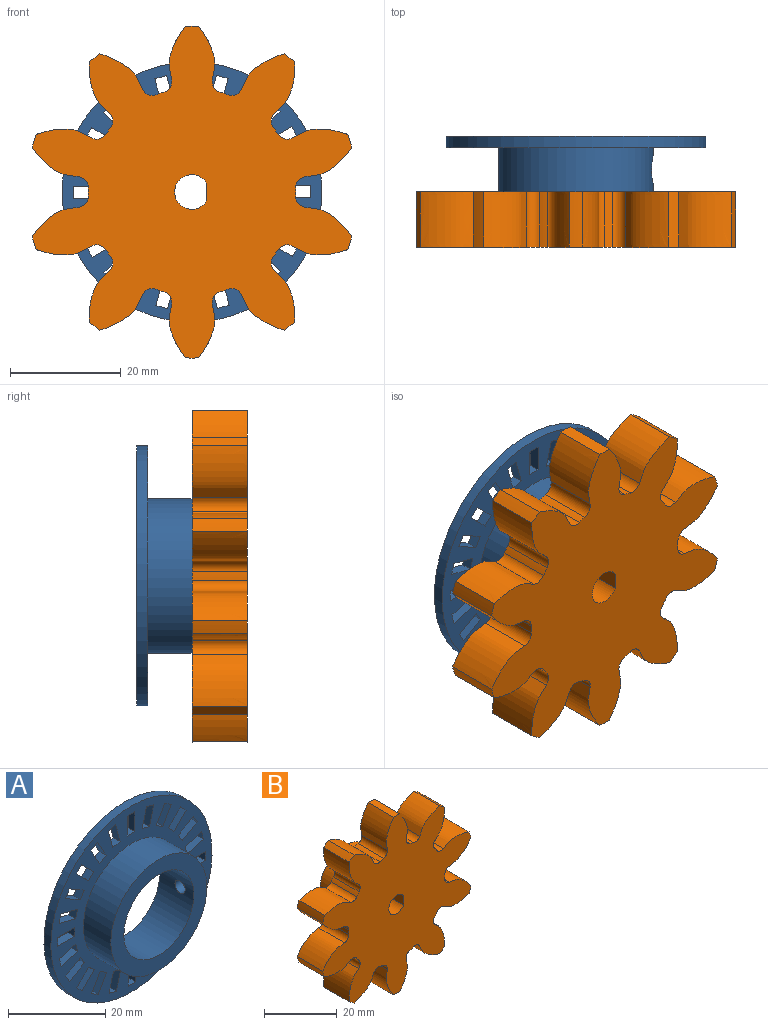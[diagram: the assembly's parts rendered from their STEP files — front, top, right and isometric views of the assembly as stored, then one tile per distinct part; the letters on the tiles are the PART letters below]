
ASSEMBLY  parts=2 mates=1
PART A: 104 faces, bbox 47x10x47 mm
  f0: cylinder r=14mm len=28mm, axis (0,1,0), area 675.5mm2, adj f99,f101,f103
  f1: cylinder r=10.2mm len=20.4mm, axis (0,1,0), area 633.8mm2, adj f100,f101,f102
  f2: plane 5x2mm, normal (0,0,-1), area 10mm2, adj f3,f98,f99,f100
  f3: plane 2.2x2mm, normal (1,0,0), area 4.4mm2, adj f2,f4,f99,f100
  f4: plane 5x2mm, normal (0,0,1), area 10mm2, adj f3,f98,f99,f100
  f5: plane 2.13x2mm, normal (-0.97,0,-0.26), area 4.4mm2, adj f6,f75,f99,f100
  f6: plane 4.83x2mm, normal (0.26,0,-0.97), area 10mm2, adj f5,f7,f99,f100
  f7: plane 2.13x2mm, normal (0.97,0,0.26), area 4.4mm2, adj f6,f75,f99,f100
  f8: plane 2x1.91mm, normal (-0.87,0,-0.5), area 4.4mm2, adj f9,f76,f99,f100
  f9: plane 4.33x2.5mm, normal (0.5,0,-0.87), area 10mm2, adj f8,f10,f99,f100
  f10: plane 2x1.91mm, normal (0.87,0,0.5), area 4.4mm2, adj f9,f76,f99,f100
  f11: plane 2x1.56mm, normal (-0.71,0,-0.71), area 4.4mm2, adj f12,f77,f99,f100
  f12: plane 3.54x3.54mm, normal (0.71,0,-0.71), area 10mm2, adj f11,f13,f99,f100
  f13: plane 2x1.56mm, normal (0.71,0,0.71), area 4.4mm2, adj f12,f77,f99,f100
  f14: plane 2x1.91mm, normal (-0.5,0,-0.87), area 4.4mm2, adj f15,f78,f99,f100
  f15: plane 4.33x2.5mm, normal (0.87,0,-0.5), area 10mm2, adj f14,f16,f99,f100
  f16: plane 2x1.91mm, normal (0.5,0,0.87), area 4.4mm2, adj f15,f78,f99,f100
  f17: plane 2.13x2mm, normal (-0.26,0,-0.97), area 4.4mm2, adj f18,f79,f99,f100
  f18: plane 4.83x2mm, normal (0.97,0,-0.26), area 10mm2, adj f17,f19,f99,f100
  f19: plane 2.13x2mm, normal (0.26,0,0.97), area 4.4mm2, adj f18,f79,f99,f100
  f20: plane 2.2x2mm, normal (0,0,-1), area 4.4mm2, adj f21,f80,f99,f100
  f21: plane 5x2mm, normal (1,0,0), area 10mm2, adj f20,f22,f99,f100
  f22: plane 2.2x2mm, normal (0,0,1), area 4.4mm2, adj f21,f80,f99,f100
  f23: plane 4.83x2mm, normal (0.97,0,0.26), area 10mm2, adj f24,f81,f99,f100
  f24: plane 2.13x2mm, normal (-0.26,0,0.97), area 4.4mm2, adj f23,f25,f99,f100
  f25: plane 4.83x2mm, normal (-0.97,0,-0.26), area 10mm2, adj f24,f81,f99,f100
  f26: plane 4.33x2.5mm, normal (0.87,0,0.5), area 10mm2, adj f27,f82,f99,f100
  f27: plane 2x1.91mm, normal (-0.5,0,0.87), area 4.4mm2, adj f26,f28,f99,f100
  f28: plane 4.33x2.5mm, normal (-0.87,0,-0.5), area 10mm2, adj f27,f82,f99,f100
  f29: plane 3.54x3.54mm, normal (0.71,0,0.71), area 10mm2, adj f30,f83,f99,f100
  f30: plane 2x1.56mm, normal (-0.71,0,0.71), area 4.4mm2, adj f29,f31,f99,f100
  f31: plane 3.54x3.54mm, normal (-0.71,0,-0.71), area 10mm2, adj f30,f83,f99,f100
  f32: plane 4.33x2.5mm, normal (0.5,0,0.87), area 10mm2, adj f33,f84,f99,f100
  f33: plane 2x1.91mm, normal (-0.87,0,0.5), area 4.4mm2, adj f32,f34,f99,f100
  f34: plane 4.33x2.5mm, normal (-0.5,0,-0.87), area 10mm2, adj f33,f84,f99,f100
  f35: plane 4.83x2mm, normal (0.26,0,0.97), area 10mm2, adj f36,f85,f99,f100
  f36: plane 2.13x2mm, normal (-0.97,0,0.26), area 4.4mm2, adj f35,f37,f99,f100
  f37: plane 4.83x2mm, normal (-0.26,0,-0.97), area 10mm2, adj f36,f85,f99,f100
  f38: plane 5x2mm, normal (0,0,1), area 10mm2, adj f39,f86,f99,f100
  f39: plane 2.2x2mm, normal (-1,0,0), area 4.4mm2, adj f38,f40,f99,f100
  f40: plane 5x2mm, normal (0,0,-1), area 10mm2, adj f39,f86,f99,f100
  f41: plane 4.83x2mm, normal (-0.26,0,0.97), area 10mm2, adj f42,f87,f99,f100
  f42: plane 2.13x2mm, normal (-0.97,0,-0.26), area 4.4mm2, adj f41,f43,f99,f100
  f43: plane 4.83x2mm, normal (0.26,0,-0.97), area 10mm2, adj f42,f87,f99,f100
  f44: plane 4.33x2.5mm, normal (-0.5,0,0.87), area 10mm2, adj f45,f88,f99,f100
  f45: plane 2x1.91mm, normal (-0.87,0,-0.5), area 4.4mm2, adj f44,f46,f99,f100
  f46: plane 4.33x2.5mm, normal (0.5,0,-0.87), area 10mm2, adj f45,f88,f99,f100
  f47: plane 3.54x3.54mm, normal (-0.71,0,0.71), area 10mm2, adj f48,f89,f99,f100
  f48: plane 2x1.56mm, normal (-0.71,0,-0.71), area 4.4mm2, adj f47,f49,f99,f100
  f49: plane 3.54x3.54mm, normal (0.71,0,-0.71), area 10mm2, adj f48,f89,f99,f100
  f50: plane 4.33x2.5mm, normal (-0.87,0,0.5), area 10mm2, adj f51,f90,f99,f100
  f51: plane 2x1.91mm, normal (-0.5,0,-0.87), area 4.4mm2, adj f50,f52,f99,f100
  f52: plane 4.33x2.5mm, normal (0.87,0,-0.5), area 10mm2, adj f51,f90,f99,f100
  f53: plane 4.83x2mm, normal (-0.97,0,0.26), area 10mm2, adj f54,f91,f99,f100
  f54: plane 2.13x2mm, normal (-0.26,0,-0.97), area 4.4mm2, adj f53,f55,f99,f100
  f55: plane 4.83x2mm, normal (0.97,0,-0.26), area 10mm2, adj f54,f91,f99,f100
  f56: plane 5x2mm, normal (-1,0,0), area 10mm2, adj f57,f92,f99,f100
  f57: plane 2.2x2mm, normal (0,0,-1), area 4.4mm2, adj f56,f58,f99,f100
  f58: plane 5x2mm, normal (1,0,0), area 10mm2, adj f57,f92,f99,f100
  f59: plane 4.83x2mm, normal (-0.97,0,-0.26), area 10mm2, adj f60,f93,f99,f100
  f60: plane 2.13x2mm, normal (0.26,0,-0.97), area 4.4mm2, adj f59,f61,f99,f100
  f61: plane 4.83x2mm, normal (0.97,0,0.26), area 10mm2, adj f60,f93,f99,f100
  f62: plane 4.33x2.5mm, normal (-0.87,0,-0.5), area 10mm2, adj f63,f94,f99,f100
  f63: plane 2x1.91mm, normal (0.5,0,-0.87), area 4.4mm2, adj f62,f64,f99,f100
  f64: plane 4.33x2.5mm, normal (0.87,0,0.5), area 10mm2, adj f63,f94,f99,f100
  f65: plane 3.54x3.54mm, normal (-0.71,0,-0.71), area 10mm2, adj f66,f95,f99,f100
  f66: plane 2x1.56mm, normal (0.71,0,-0.71), area 4.4mm2, adj f65,f67,f99,f100
  f67: plane 3.54x3.54mm, normal (0.71,0,0.71), area 10mm2, adj f66,f95,f99,f100
  f68: plane 4.33x2.5mm, normal (-0.5,0,-0.87), area 10mm2, adj f69,f96,f99,f100
  f69: plane 2x1.91mm, normal (0.87,0,-0.5), area 4.4mm2, adj f68,f70,f99,f100
  f70: plane 4.33x2.5mm, normal (0.5,0,0.87), area 10mm2, adj f69,f96,f99,f100
  f71: plane 4.83x2mm, normal (-0.26,0,-0.97), area 10mm2, adj f72,f97,f99,f100
  f72: plane 2.13x2mm, normal (0.97,0,-0.26), area 4.4mm2, adj f71,f73,f99,f100
  f73: plane 4.83x2mm, normal (0.26,0,0.97), area 10mm2, adj f72,f97,f99,f100
  f74: cylinder r=23.5mm len=47mm, axis (0,1,0), area 295.3mm2, adj f99,f100
  f75: plane 4.83x2mm, normal (-0.26,0,0.97), area 10mm2, adj f5,f7,f99,f100
  f76: plane 4.33x2.5mm, normal (-0.5,0,0.87), area 10mm2, adj f8,f10,f99,f100
  f77: plane 3.54x3.54mm, normal (-0.71,0,0.71), area 10mm2, adj f11,f13,f99,f100
  f78: plane 4.33x2.5mm, normal (-0.87,0,0.5), area 10mm2, adj f14,f16,f99,f100
  f79: plane 4.83x2mm, normal (-0.97,0,0.26), area 10mm2, adj f17,f19,f99,f100
  f80: plane 5x2mm, normal (-1,0,0), area 10mm2, adj f20,f22,f99,f100
  f81: plane 2.13x2mm, normal (0.26,0,-0.97), area 4.4mm2, adj f23,f25,f99,f100
  f82: plane 2x1.91mm, normal (0.5,0,-0.87), area 4.4mm2, adj f26,f28,f99,f100
  f83: plane 2x1.56mm, normal (0.71,0,-0.71), area 4.4mm2, adj f29,f31,f99,f100
  f84: plane 2x1.91mm, normal (0.87,0,-0.5), area 4.4mm2, adj f32,f34,f99,f100
  f85: plane 2.13x2mm, normal (0.97,0,-0.26), area 4.4mm2, adj f35,f37,f99,f100
  f86: plane 2.2x2mm, normal (1,0,0), area 4.4mm2, adj f38,f40,f99,f100
  f87: plane 2.13x2mm, normal (0.97,0,0.26), area 4.4mm2, adj f41,f43,f99,f100
  f88: plane 2x1.91mm, normal (0.87,0,0.5), area 4.4mm2, adj f44,f46,f99,f100
  f89: plane 2x1.56mm, normal (0.71,0,0.71), area 4.4mm2, adj f47,f49,f99,f100
  f90: plane 2x1.91mm, normal (0.5,0,0.87), area 4.4mm2, adj f50,f52,f99,f100
  f91: plane 2.13x2mm, normal (0.26,0,0.97), area 4.4mm2, adj f53,f55,f99,f100
  f92: plane 2.2x2mm, normal (0,0,1), area 4.4mm2, adj f56,f58,f99,f100
  f93: plane 2.13x2mm, normal (-0.26,0,0.97), area 4.4mm2, adj f59,f61,f99,f100
  f94: plane 2x1.91mm, normal (-0.5,0,0.87), area 4.4mm2, adj f62,f64,f99,f100
  f95: plane 2x1.56mm, normal (-0.71,0,0.71), area 4.4mm2, adj f65,f67,f99,f100
  f96: plane 2x1.91mm, normal (-0.87,0,0.5), area 4.4mm2, adj f68,f70,f99,f100
  f97: plane 2.13x2mm, normal (-0.97,0,0.26), area 4.4mm2, adj f71,f73,f99,f100
  f98: plane 2.2x2mm, normal (-1,0,0), area 4.4mm2, adj f2,f4,f99,f100
  f99: plane 47x47mm, normal (0,-1,0), area 855.2mm2, adj f0,f2,f3,f4,f5,f6,f7,f8
  f100: plane 47x47mm, normal (0,1,0), area 1144.1mm2, adj f1,f2,f3,f4,f5,f6,f7,f8
  f101: plane 28x28mm, normal (0,-1,0), area 288.9mm2, adj f0,f1
  f102: cylinder r=1.5mm len=3mm, axis (-1,0,0), area 22.4mm2, adj f1,f103
  f103: bspline ~6.26x5.72mm, area 27.2mm2, adj f0,f102
PART B: 74 faces, bbox 57.9x20x60.1 mm
  f0: cylinder r=10mm len=20mm, axis (0,-1,0), area 621.2mm2, adj f2,f65,f72
  f1: plane 60.12x57.93mm, normal (0,-1,0), area 1850.8mm2, adj f3,f4,f5,f6,f7,f8,f9,f10
  f2: plane 60.12x57.93mm, normal (0,1,0), area 1566.5mm2, adj f0,f3,f4,f5,f6,f7,f8,f9
  f3: cylinder r=30mm len=10mm, axis (0,1,0), area 24.1mm2, adj f1,f2,f53,f60
  f4: cylinder r=30mm len=10mm, axis (0,1,0), area 24.1mm2, adj f1,f2,f13,f55
  f5: cylinder r=30mm len=10mm, axis (0,1,0), area 24.1mm2, adj f1,f2,f43,f50
  f6: cylinder r=30mm len=10mm, axis (0,1,0), area 24.1mm2, adj f1,f2,f45,f58
  f7: cylinder r=30mm len=10mm, axis (0,1,0), area 24.1mm2, adj f1,f2,f33,f40
  f8: cylinder r=30mm len=10mm, axis (0,1,0), area 24.1mm2, adj f1,f2,f28,f35
  f9: cylinder r=30mm len=10mm, axis (0,1,0), area 24.1mm2, adj f1,f2,f23,f30
  f10: cylinder r=30mm len=10mm, axis (0,1,0), area 24.1mm2, adj f1,f2,f25,f48
  f11: cylinder r=30mm len=10mm, axis (0,1,0), area 24.1mm2, adj f1,f2,f20,f38
  f12: cylinder r=30mm len=10mm, axis (0,1,0), area 24.1mm2, adj f1,f2,f15,f18
  f13: extruded ~10x8.48mm, area 105.4mm2, adj f1,f2,f4,f16
  f14: cylinder r=18.75mm len=10mm, axis (0,1,0), area 15.2mm2, adj f1,f2,f16,f17
  f15: extruded ~10x8.48mm, area 105.4mm2, adj f1,f2,f12,f17
  f16: cylinder r=1.92mm len=10mm, axis (0,1,0), area 28.5mm2, adj f1,f2,f13,f14
  f17: cylinder r=1.92mm len=10mm, axis (0,1,0), area 28.5mm2, adj f1,f2,f14,f15
  f18: extruded ~10.02x10mm, area 105.4mm2, adj f1,f2,f12,f21
  f19: cylinder r=18.75mm len=10mm, axis (0,1,0), area 15.2mm2, adj f1,f2,f21,f22
  f20: extruded ~10x9.33mm, area 105.4mm2, adj f1,f2,f11,f22
  f21: cylinder r=1.92mm len=10mm, axis (0,1,0), area 28.5mm2, adj f1,f2,f18,f19
  f22: cylinder r=1.92mm len=10mm, axis (0,1,0), area 28.5mm2, adj f1,f2,f19,f20
  f23: extruded ~10x8.48mm, area 105.4mm2, adj f1,f2,f9,f26
  f24: cylinder r=18.75mm len=10mm, axis (0,1,0), area 15.2mm2, adj f1,f2,f26,f27
  f25: extruded ~10x8.48mm, area 105.4mm2, adj f1,f2,f10,f27
  f26: cylinder r=1.92mm len=10mm, axis (0,1,0), area 28.5mm2, adj f1,f2,f23,f24
  f27: cylinder r=1.92mm len=10mm, axis (0,1,0), area 28.5mm2, adj f1,f2,f24,f25
  f28: extruded ~10x9.33mm, area 105.4mm2, adj f1,f2,f8,f31
  f29: cylinder r=18.75mm len=10mm, axis (0,1,0), area 15.2mm2, adj f1,f2,f31,f32
  f30: extruded ~10.02x10mm, area 105.4mm2, adj f1,f2,f9,f32
  f31: cylinder r=1.92mm len=10mm, axis (0,1,0), area 28.5mm2, adj f1,f2,f28,f29
  f32: cylinder r=1.92mm len=10mm, axis (0,1,0), area 28.5mm2, adj f1,f2,f29,f30
  f33: extruded ~10x9.72mm, area 105.4mm2, adj f1,f2,f7,f36
  f34: cylinder r=18.75mm len=10mm, axis (0,1,0), area 15.2mm2, adj f1,f2,f36,f37
  f35: extruded ~10x7.73mm, area 105.4mm2, adj f1,f2,f8,f37
  f36: cylinder r=1.92mm len=10mm, axis (0,1,0), area 28.5mm2, adj f1,f2,f33,f34
  f37: cylinder r=1.92mm len=10mm, axis (0,1,0), area 28.5mm2, adj f1,f2,f34,f35
  f38: extruded ~10x7.73mm, area 105.4mm2, adj f1,f2,f11,f41
  f39: cylinder r=18.75mm len=10mm, axis (0,1,0), area 15.2mm2, adj f1,f2,f41,f42
  f40: extruded ~10x9.72mm, area 105.4mm2, adj f1,f2,f7,f42
  f41: cylinder r=1.92mm len=10mm, axis (0,1,0), area 28.5mm2, adj f1,f2,f38,f39
  f42: cylinder r=1.92mm len=10mm, axis (0,1,0), area 28.5mm2, adj f1,f2,f39,f40
  f43: extruded ~10x7.73mm, area 105.4mm2, adj f1,f2,f5,f46
  f44: cylinder r=18.75mm len=10mm, axis (0,1,0), area 15.2mm2, adj f1,f2,f46,f47
  f45: extruded ~10x9.72mm, area 105.4mm2, adj f1,f2,f6,f47
  f46: cylinder r=1.92mm len=10mm, axis (0,1,0), area 28.5mm2, adj f1,f2,f43,f44
  f47: cylinder r=1.92mm len=10mm, axis (0,1,0), area 28.5mm2, adj f1,f2,f44,f45
  f48: extruded ~10.02x10mm, area 105.4mm2, adj f1,f2,f10,f51
  f49: cylinder r=18.75mm len=10mm, axis (0,1,0), area 15.2mm2, adj f1,f2,f51,f52
  f50: extruded ~10x9.33mm, area 105.4mm2, adj f1,f2,f5,f52
  f51: cylinder r=1.92mm len=10mm, axis (0,1,0), area 28.5mm2, adj f1,f2,f48,f49
  f52: cylinder r=1.92mm len=10mm, axis (0,1,0), area 28.5mm2, adj f1,f2,f49,f50
  f53: extruded ~10x9.33mm, area 105.4mm2, adj f1,f2,f3,f56
  f54: cylinder r=18.75mm len=10mm, axis (0,1,0), area 15.2mm2, adj f1,f2,f56,f57
  f55: extruded ~10.02x10mm, area 105.4mm2, adj f1,f2,f4,f57
  f56: cylinder r=1.92mm len=10mm, axis (0,1,0), area 28.5mm2, adj f1,f2,f53,f54
  f57: cylinder r=1.92mm len=10mm, axis (0,1,0), area 28.5mm2, adj f1,f2,f54,f55
  f58: extruded ~10x9.72mm, area 105.4mm2, adj f1,f2,f6,f61
  f59: cylinder r=18.75mm len=10mm, axis (0,1,0), area 15.2mm2, adj f1,f2,f61,f62
  f60: extruded ~10x7.73mm, area 105.4mm2, adj f1,f2,f3,f62
  f61: cylinder r=1.92mm len=10mm, axis (0,1,0), area 28.5mm2, adj f1,f2,f58,f59
  f62: cylinder r=1.92mm len=10mm, axis (0,1,0), area 28.5mm2, adj f1,f2,f59,f60
  f63: plane 20x3.15mm, normal (-1,0,0), area 55.9mm2, adj f1,f64,f65,f73
  f64: cylinder r=3.12mm len=20mm, axis (0,-1,0), area 326.7mm2, adj f1,f63,f65
  f65: plane 20x20mm, normal (0,1,0), area 267.3mm2, adj f0,f63,f64,f66,f67,f70,f71
  f66: plane 7.65x3mm, normal (0,0,1), area 22.9mm2, adj f65,f69,f70,f71
  f67: plane 7.65x3mm, normal (0,0,-1), area 22.9mm2, adj f65,f68,f70,f71
  f68: plane 3x2.85mm, normal (0,0.87,-0.5), area 9.9mm2, adj f67,f69,f70,f71
  f69: plane 3x2.85mm, normal (0,0.87,0.5), area 9.9mm2, adj f66,f68,f70,f71
  f70: plane 9.29x5.7mm, normal (1,0,0), area 41.2mm2, adj f65,f66,f67,f68,f69,f73
  f71: plane 9.29x5.7mm, normal (-1,0,0), area 41.2mm2, adj f65,f66,f67,f68,f69,f72
  f72: cylinder r=1.5mm len=3mm, axis (-1,0,0), area 25.4mm2, adj f0,f71
  f73: cylinder r=1.5mm len=3mm, axis (-1,0,0), area 14.6mm2, adj f63,f70
PLACE A t=(8.62,-3.06,20.47)mm
PLACE B t=(8.62,-3.06,20.47)mm
MATE fastened B.f64 <-> A.f0  axis (0,-1,0) through (8.62,6.94,20.47)mm
